# Revit family: Toilet_Seat-Elongated_Closed_Front-KOHLER-PATIO_REGULAR-K-4837IN
name_source: partatom
category: Specialty Equipment
revit_build: Autodesk Revit 2017 (Build: 20160225_1515(x64)
units: mm (PartAtom-declared; Revit-internal decimal feet)

## family parameters
Cut with Voids When Loaded = No
Host = Face
OmniClass Number = 23.31.25.00
OmniClass Title = Toilet and Bath Specialties
Part Type = Normal
Room Calculation Point = No
Round Connector Dimension = Use Diameter
Shared = No

## types (2) — shared parameters
ADA Compliant = No
Assembly Code = C1030200
Date Modified = 12/24/2020
Default Elevation = 0"
Description = Close toilet seat
Height = 2 3/8"
Length = 18 1/8"
Manufacturer = KOHLER Co.
Master Format 2014 = 10 28 00
Master Format 2014 Name = Toilet, Bath, and Laundry Accessories
Material = Plastic
Product Name = PATIO_REGULAR
URL = https://www.kohler.co.in
WaterSense Certified = No
Width = 14 13/16"

## per-type parameters (varying)
| type | Finish | Model | Type |
| 0- White | Kohler-Plastic-0-White | K-4837IN-0 | 1 |
| 96- Biscuit | Kohler-Plastic-96-Biscuit | K-4837IN-96 | 2 |

## geometry (parser evidence)
native form markers: Sweep x6
no freeform markers — native parametric forms only
